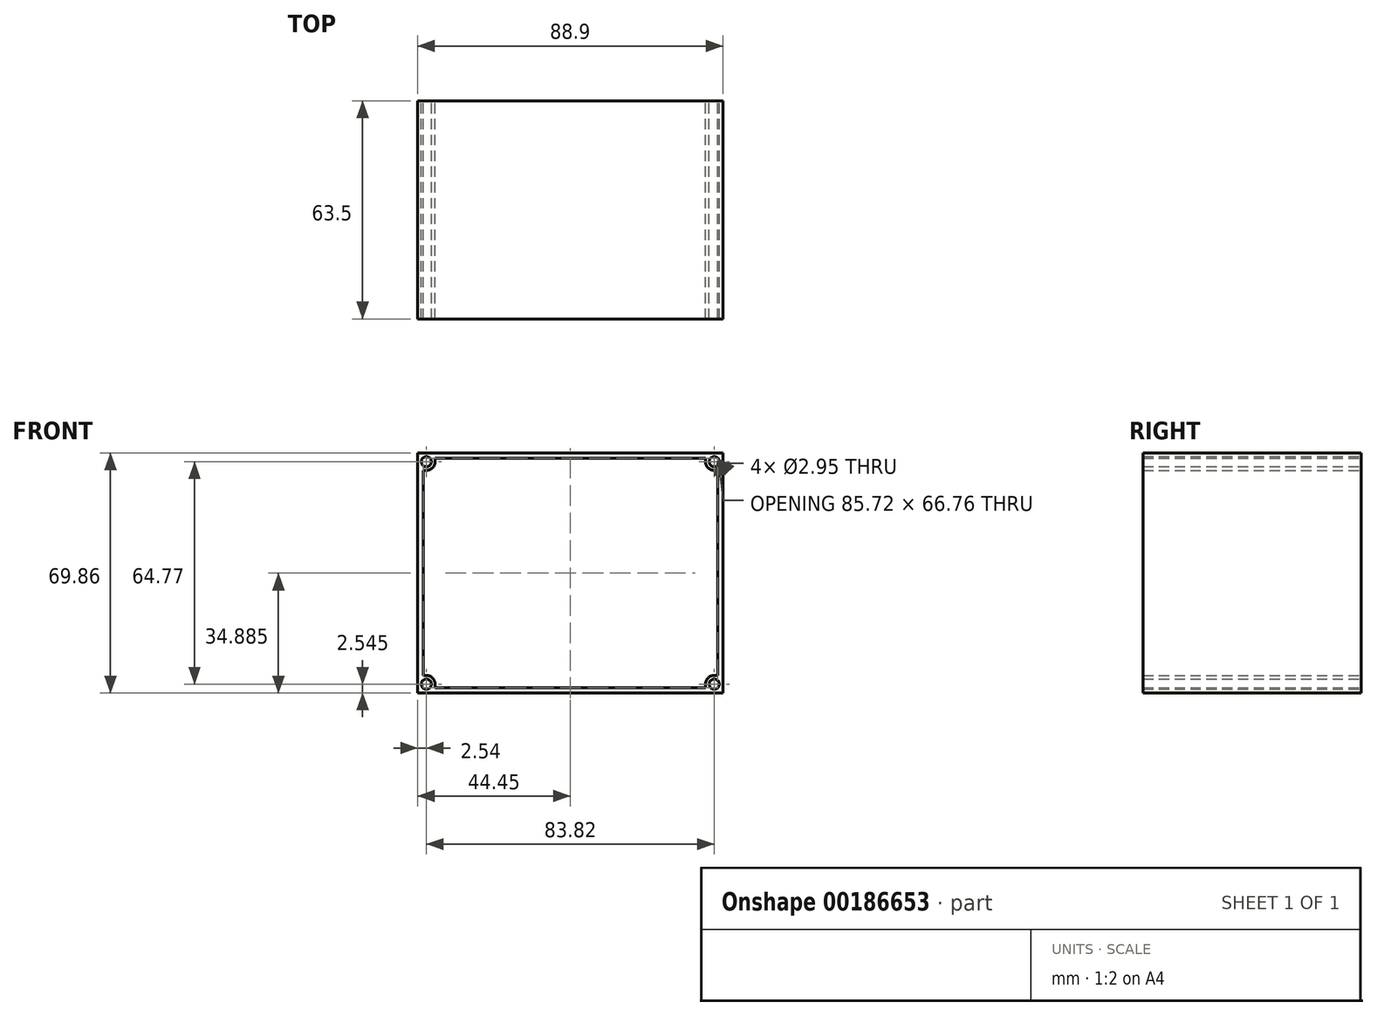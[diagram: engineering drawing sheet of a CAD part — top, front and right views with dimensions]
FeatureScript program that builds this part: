
annotation { "Feature Type Name" : "Feature", "Feature Type Description" : "" }
export const myFeature = defineFeature(function(context is Context, id is Id, definition is map)
    precondition{}
    {
        {
            var Q0;
            Q0=qCreatedBy(makeId("Front.planeOp"),FACE);
            var sketch = newSketch(context, id + "F0", { "sketchPlane" : qUnion([Q0])});
            skLineSegment(sketch, "E0.bottom", {"start": v(-44.45, 34.93) * mm, "end": v(44.45, 34.93) * mm});
            skLineSegment(sketch, "E0.top", {"start": v(-44.45, -34.92) * mm, "end": v(44.45, -34.92) * mm});
            skLineSegment(sketch, "E0.left", {"start": v(-44.45, 34.93) * mm, "end": v(-44.45, -34.92) * mm});
            skLineSegment(sketch, "E0.right", {"start": v(44.45, 34.93) * mm, "end": v(44.45, -34.92) * mm});
            skPoint(sketch, "E0.middle", {"position": v(0, 0) * mm});
            skLineSegment(sketch, "E1.top", {"start": v(-39.37, -33.43) * mm, "end": v(39.37, -33.43) * mm});
            skLineSegment(sketch, "E2.bottom", {"start": v(-44.45, 34.93) * mm, "end": v(-39.37, 34.93) * mm});
            skLineSegment(sketch, "E2.top", {"start": v(-42.86, 29.85) * mm, "end": v(-41.91, 29.85) * mm});
            skLineSegment(sketch, "E2.left", {"start": v(-44.45, 34.93) * mm, "end": v(-44.45, 29.85) * mm});
            skLineSegment(sketch, "E2.right", {"start": v(-39.37, 33.34) * mm, "end": v(-39.37, 32.39) * mm});
            skLineSegment(sketch, "E3", {"start": v(-39.37, 34.93) * mm, "end": v(-44.45, 29.85) * mm, "construction": true});
            skPoint(sketch, "E4.visualSharp", {"position": v(-39.37, 29.85) * mm});
            skArc(sketch, "E4.filletArc", {"start": v(-41.91, 29.85) * mm, "mid": v(-40.11, 30.59) * mm, "end": v(-39.37, 32.39) * mm});
            skLineSegment(sketch, "E5.trimOffspring", {"start": v(-39.37, 33.34) * mm, "end": v(39.37, 33.34) * mm});
            skLineSegment(sketch, "E6.trimOffspring", {"start": v(-42.86, 29.85) * mm, "end": v(-42.86, -29.84) * mm});
            skLineSegment(sketch, "E7.bottom", {"start": v(44.45, 34.93) * mm, "end": v(39.37, 34.93) * mm});
            skLineSegment(sketch, "E7.top", {"start": v(42.86, 29.85) * mm, "end": v(41.91, 29.85) * mm});
            skLineSegment(sketch, "E7.left", {"start": v(44.45, 34.93) * mm, "end": v(44.45, 29.85) * mm});
            skLineSegment(sketch, "E7.right", {"start": v(39.37, 33.34) * mm, "end": v(39.37, 32.39) * mm});
            skLineSegment(sketch, "E8", {"start": v(44.45, 34.93) * mm, "end": v(39.37, 29.85) * mm, "construction": true});
            skLineSegment(sketch, "E9", {"start": v(39.37, 34.93) * mm, "end": v(44.45, 29.85) * mm, "construction": true});
            skCircle(sketch, "E10", {"center": v(41.91, 32.39) * mm, "radius": 1.47 * mm});
            skPoint(sketch, "E11.visualSharp", {"position": v(39.37, 29.85) * mm});
            skArc(sketch, "E11.filletArc", {"start": v(39.37, 32.39) * mm, "mid": v(40.11, 30.59) * mm, "end": v(41.91, 29.85) * mm});
            skLineSegment(sketch, "E12.trimOffspring", {"start": v(42.86, 29.85) * mm, "end": v(42.86, -29.84) * mm});
            skLineSegment(sketch, "E13.bottom", {"start": v(44.45, -34.92) * mm, "end": v(39.37, -34.92) * mm});
            skLineSegment(sketch, "E13.top", {"start": v(42.86, -29.84) * mm, "end": v(41.9, -29.84) * mm});
            skLineSegment(sketch, "E13.left", {"start": v(44.45, -34.92) * mm, "end": v(44.45, -29.84) * mm});
            skLineSegment(sketch, "E13.right", {"start": v(39.37, -34.92) * mm, "end": v(39.37, -32.38) * mm});
            skLineSegment(sketch, "E14", {"start": v(44.45, -34.92) * mm, "end": v(39.37, -29.84) * mm, "construction": true});
            skLineSegment(sketch, "E15", {"start": v(44.45, -29.84) * mm, "end": v(39.37, -34.92) * mm, "construction": true});
            skCircle(sketch, "E16", {"center": v(41.9, -32.38) * mm, "radius": 1.47 * mm});
            skPoint(sketch, "E17.visualSharp", {"position": v(39.37, -29.84) * mm});
            skArc(sketch, "E17.filletArc", {"start": v(41.9, -29.84) * mm, "mid": v(40.11, -30.59) * mm, "end": v(39.37, -32.38) * mm});
            skPoint(sketch, "E18.orphan", {"position": v(42.95, -33.43) * mm});
            skPoint(sketch, "E1.right.start.orphan", {"position": v(42.86, 33.43) * mm});
            skLineSegment(sketch, "E19.bottom", {"start": v(-44.45, -34.92) * mm, "end": v(-39.37, -34.92) * mm});
            skLineSegment(sketch, "E19.top", {"start": v(-42.86, -29.84) * mm, "end": v(-41.91, -29.84) * mm});
            skLineSegment(sketch, "E19.left", {"start": v(-44.45, -34.92) * mm, "end": v(-44.45, -29.84) * mm});
            skLineSegment(sketch, "E19.right", {"start": v(-39.37, -33.43) * mm, "end": v(-39.37, -32.38) * mm});
            skLineSegment(sketch, "E20", {"start": v(-44.45, -34.92) * mm, "end": v(-39.37, -29.84) * mm, "construction": true});
            skLineSegment(sketch, "E21", {"start": v(-39.37, -34.92) * mm, "end": v(-44.45, -29.84) * mm, "construction": true});
            skCircle(sketch, "E22", {"center": v(-41.91, -32.38) * mm, "radius": 1.47 * mm});
            skPoint(sketch, "E23.visualSharp", {"position": v(-39.37, -29.84) * mm});
            skArc(sketch, "E23.filletArc", {"start": v(-39.37, -32.38) * mm, "mid": v(-40.11, -30.59) * mm, "end": v(-41.91, -29.84) * mm});
            skPoint(sketch, "E24.trimOffspring.end.orphan", {"position": v(-42.86, -33.43) * mm});
            skLineSegment(sketch, "E25", {"start": v(-44.45, 29.85) * mm, "end": v(-39.37, 29.85) * mm, "construction": true});
            skLineSegment(sketch, "E26", {"start": v(-39.37, 34.93) * mm, "end": v(-39.37, 29.85) * mm, "construction": true});
            skLineSegment(sketch, "E27", {"start": v(-39.37, 29.85) * mm, "end": v(-44.45, 34.93) * mm, "construction": true});
            skCircle(sketch, "E28", {"center": v(-41.91, 32.39) * mm, "radius": 1.47 * mm});
            skSolve(sketch);
        }
        {
            var Q0;
            Q0=makeQuery(id+"F0.imprint","IMPRINT",FACE,{"disambiguationData":[TD([[makeQuery(id+"F0.imprint","IMPRINT",EDGE,{"derivedFrom":sQuery(id+"F0.wireOp",EDGE,"E0.bottom")}),-1.0]])]});
            extrude(context, id + "F1", {"entities" : qUnion([Q0]), "endBound" : BoundingType.SYMMETRIC, "depth" : 63.5 * mm});
        }
    });
